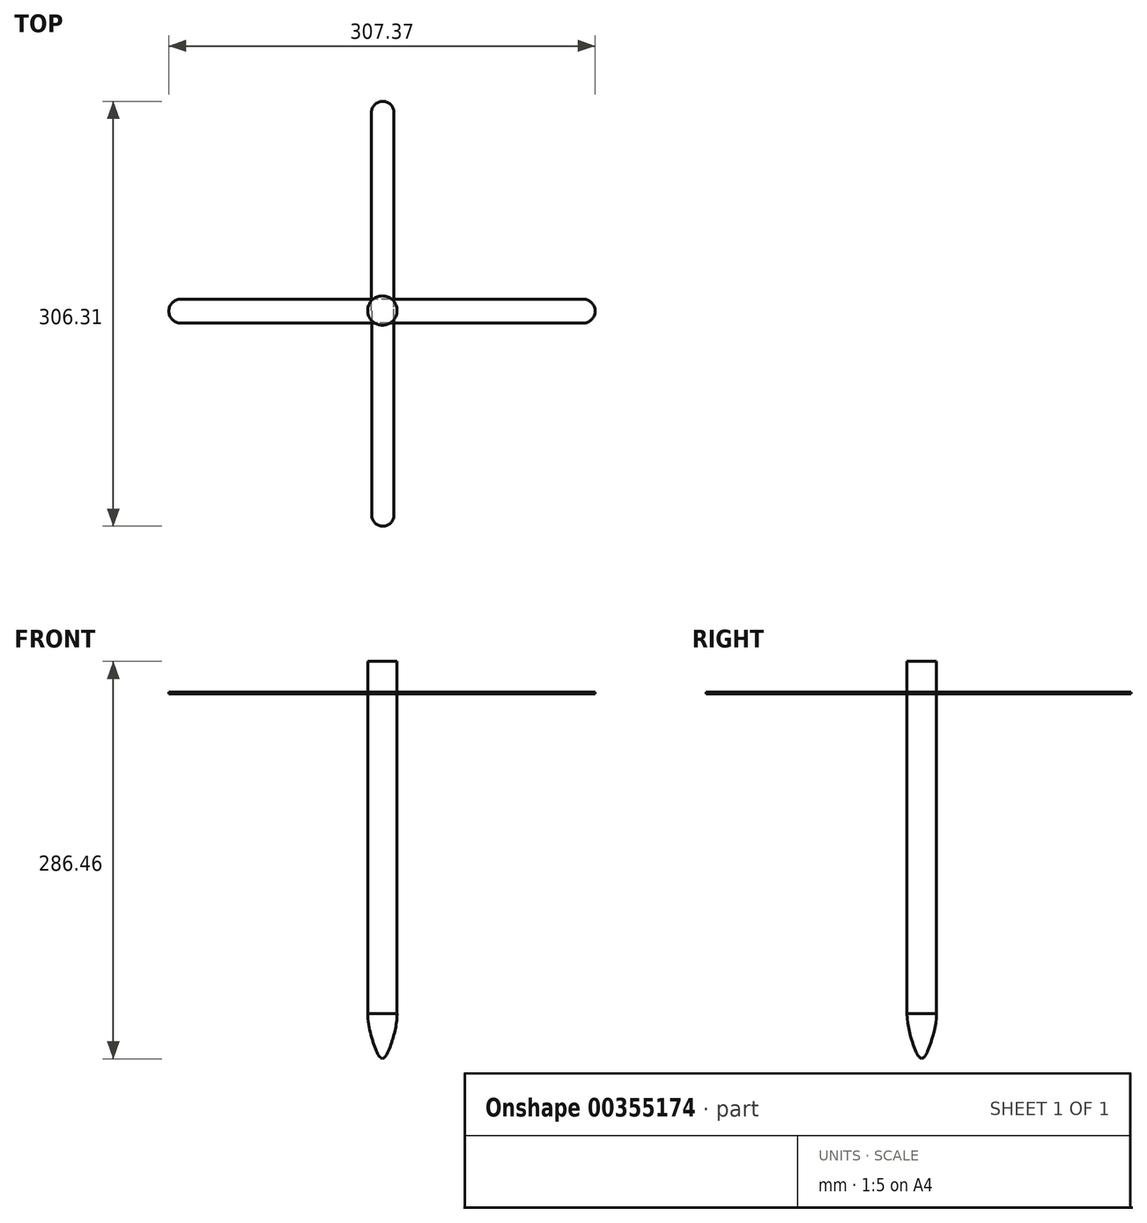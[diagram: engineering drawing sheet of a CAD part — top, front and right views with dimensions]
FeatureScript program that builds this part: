
annotation { "Feature Type Name" : "Feature", "Feature Type Description" : "" }
export const myFeature = defineFeature(function(context is Context, id is Id, definition is map)
    precondition{}
    {
        {
            var Q0;
            Q0=qCreatedBy(makeId("Top.planeOp"),FACE);
            var sketch = newSketch(context, id + "F0", { "sketchPlane" : qUnion([Q0])});
            skCircle(sketch, "E0", {"center": v(0, 0) * mm, "radius": 10.59 * mm});
            skSolve(sketch);
        }
        {
            var Q0;
            Q0=makeQuery(id+"F0.imprint","IMPRINT",FACE,{"disambiguationData":[TD([[makeQuery(id+"F0.imprint","IMPRINT",EDGE,{"derivedFrom":sQuery(id+"F0.wireOp",EDGE,"E0")}),1.0]])]});
            extrude(context, id + "F1", {"entities" : qUnion([Q0]), "endBound" : BoundingType.SYMMETRIC, "depth" : 254 * mm});
        }
        {
            var Q0;
            Q0=qCreatedBy(makeId("Top.planeOp"),FACE);
            cPlane(context, id + "F2", {"entities" : qUnion([Q0]), "cplaneType" : CPlaneType.OFFSET, "offset" : 104.9 * mm, "width" : 152.4 * mm, "height" : 152.4 * mm});
        }
        {
            var Q0;
            Q0=qCreatedBy(id+"F2.planeOp",FACE);
            var sketch = newSketch(context, id + "F3", { "sketchPlane" : qUnion([Q0])});
            skLineSegment(sketch, "E1.bottom", {"start": v(0, 8.19) * mm, "end": v(-145.4, 8.19) * mm});
            skLineSegment(sketch, "E1.top", {"start": v(0, -9) * mm, "end": v(-145.4, -9) * mm});
            skLineSegment(sketch, "E1.left", {"start": v(0, 8.19) * mm, "end": v(0, -9) * mm});
            skLineSegment(sketch, "E1.right", {"start": v(-145.4, 8.19) * mm, "end": v(-145.4, -9) * mm});
            skLineSegment(sketch, "E2.left", {"start": v(0, 8.19) * mm, "end": v(0, 8.19) * mm});
            skLineSegment(sketch, "E2.right", {"start": v(-145.4, 8.19) * mm, "end": v(-145.4, 8.19) * mm});
            skLineSegment(sketch, "E3.bottom", {"start": v(144.78, 8.19) * mm, "end": v(-0.62, 8.19) * mm});
            skLineSegment(sketch, "E3.top", {"start": v(144.78, -9) * mm, "end": v(-0.62, -9) * mm});
            skLineSegment(sketch, "E3.left", {"start": v(144.78, 8.19) * mm, "end": v(144.78, -9) * mm});
            skLineSegment(sketch, "E3.right", {"start": v(-0.62, 8.19) * mm, "end": v(-0.62, -9) * mm});
            skLineSegment(sketch, "E4.left", {"start": v(-173.38, 15.87) * mm, "end": v(-173.38, 15.87) * mm});
            skLineSegment(sketch, "E4.right", {"start": v(-318.77, 15.87) * mm, "end": v(-318.77, 15.87) * mm});
            skArc(sketch, "E5", {"start": v(-145.4, 8.19) * mm, "mid": v(-154, -0.41) * mm, "end": v(-145.4, -9) * mm});
            skArc(sketch, "E6", {"start": v(144.78, 8.19) * mm, "mid": v(153.38, -0.41) * mm, "end": v(144.78, -9) * mm});
            skLineSegment(sketch, "E7.bottom", {"start": v(8.37, 0) * mm, "end": v(-7.9, 0) * mm});
            skLineSegment(sketch, "E7.top", {"start": v(8.37, 142.74) * mm, "end": v(-7.9, 142.74) * mm});
            skLineSegment(sketch, "E7.left", {"start": v(8.37, 0) * mm, "end": v(8.37, 142.74) * mm});
            skLineSegment(sketch, "E7.right", {"start": v(-7.9, 0) * mm, "end": v(-7.9, 142.74) * mm});
            skLineSegment(sketch, "E8.bottom", {"start": v(8.37, 0) * mm, "end": v(-7.65, 0) * mm});
            skLineSegment(sketch, "E8.top", {"start": v(8.37, -147.43) * mm, "end": v(-7.65, -147.43) * mm});
            skLineSegment(sketch, "E8.left", {"start": v(8.37, 0) * mm, "end": v(8.37, -147.43) * mm});
            skLineSegment(sketch, "E8.right", {"start": v(-7.65, 0) * mm, "end": v(-7.65, -147.43) * mm});
            skArc(sketch, "E9", {"start": v(-7.9, 142.74) * mm, "mid": v(0.24, 150.87) * mm, "end": v(8.37, 142.74) * mm});
            skArc(sketch, "E10", {"start": v(-7.65, -147.43) * mm, "mid": v(0.36, -155.44) * mm, "end": v(8.37, -147.43) * mm});
            skSolve(sketch);
        }
        {
            var Q0;
            {var subQ1=sQuery(id+"F3.wireOp",EDGE,"E1.right");Q0=makeQuery(id+"F3.imprint","IMPRINT",FACE,{"disambiguationData":[TD([[makeQuery(id+"F3.imprint","IMPRINT",EDGE,{"derivedFrom":subQ1}),1.0]])]});}
            var Q1;
            {var subQ0=sQuery(id+"F3.wireOp",EDGE,"E7.top");Q1=makeQuery(id+"F3.imprint","IMPRINT",FACE,{"disambiguationData":[TD([[makeQuery(id+"F3.imprint","IMPRINT",EDGE,{"derivedFrom":subQ0}),1.0]])]});}
            var Q2;
            {var subQ2=sQuery(id+"F3.wireOp",EDGE,"E3.left");Q2=makeQuery(id+"F3.imprint","IMPRINT",FACE,{"disambiguationData":[TD([[makeQuery(id+"F3.imprint","IMPRINT",EDGE,{"derivedFrom":subQ2}),-1.0]])]});}
            var Q3;
            {var subQ0=sQuery(id+"F3.wireOp",EDGE,"E8.top");Q3=makeQuery(id+"F3.imprint","IMPRINT",FACE,{"disambiguationData":[TD([[makeQuery(id+"F3.imprint","IMPRINT",EDGE,{"derivedFrom":subQ0}),-1.0]])]});}
            var Q4;
            Q4=makeQuery(id+"F3.imprint","IMPRINT",FACE,{"disambiguationData":[TD([[makeQuery(id+"F3.imprint","IMPRINT",EDGE,{"derivedFrom":sQuery(id+"F3.wireOp",EDGE,"E8.top")}),1.0]])]});
            var Q5;
            Q5=makeQuery(id+"F3.imprint","IMPRINT",FACE,{"disambiguationData":[TD([[makeQuery(id+"F3.imprint","IMPRINT",EDGE,{"derivedFrom":sQuery(id+"F3.wireOp",EDGE,"E3.left")}),1.0]])]});
            var Q6;
            Q6=makeQuery(id+"F3.imprint","IMPRINT",FACE,{"disambiguationData":[TD([[makeQuery(id+"F3.imprint","IMPRINT",EDGE,{"derivedFrom":sQuery(id+"F3.wireOp",EDGE,"E1.right")}),-1.0]])]});
            var Q7;
            Q7=makeQuery(id+"F3.imprint","IMPRINT",FACE,{"disambiguationData":[TD([[makeQuery(id+"F3.imprint","IMPRINT",EDGE,{"derivedFrom":sQuery(id+"F3.wireOp",EDGE,"E7.top")}),-1.0]])]});
            extrude(context, id + "F4", {"entities" : qUnion([Q0, Q1, Q2, Q3, Q4, Q5, Q6, Q7]), "oppositeDirection" : true, "depth" : 1.27 * mm});
        }
        {
            var Q0;
            Q0=qCreatedBy(makeId("Front.planeOp"),FACE);
            var sketch = newSketch(context, id + "F5", { "sketchPlane" : qUnion([Q0])});
            skLineSegment(sketch, "E11", {"start": v(0, -127.02) * mm, "end": v(-10.62, -127.02) * mm});
            skLineSegment(sketch, "E12", {"start": v(-10.62, -127.02) * mm, "end": v(0, -159.46) * mm});
            skLineSegment(sketch, "E13", {"start": v(0, -159.46) * mm, "end": v(0, -127.02) * mm});
            skFitSpline(sketch, "E14", {"points": [v(-10.62, -127.02) * mm, v(-4.24, -154.15) * mm, v(0, -159.46) * mm], "startDerivative": vector(-0.18, -41.5) * mm, "endDerivative": vector(19.4, -11.58) * mm});
            skSolve(sketch);
        }
        {
            var Q0;
            Q0=makeQuery(id+"F5.imprint","IMPRINT",FACE,{"disambiguationData":[TD([[makeQuery(id+"F5.imprint","IMPRINT",EDGE,{"derivedFrom":sQuery(id+"F5.wireOp",EDGE,"E12")}),-1.0]])]});
            var Q1;
            Q1=makeQuery(id+"F5.imprint","IMPRINT",FACE,{"disambiguationData":[TD([[makeQuery(id+"F5.imprint","IMPRINT",EDGE,{"derivedFrom":sQuery(id+"F5.wireOp",EDGE,"E11")}),1.0]])]});
            var Q2;
            Q2=sQuery(id+"F5.wireOp",EDGE,"E13");
            revolve(context, id + "F6", {"entities" : qUnion([Q0, Q1]), "axis" : qUnion([Q2]), "revolveType" : RevolveType.FULL});
        }
    });
